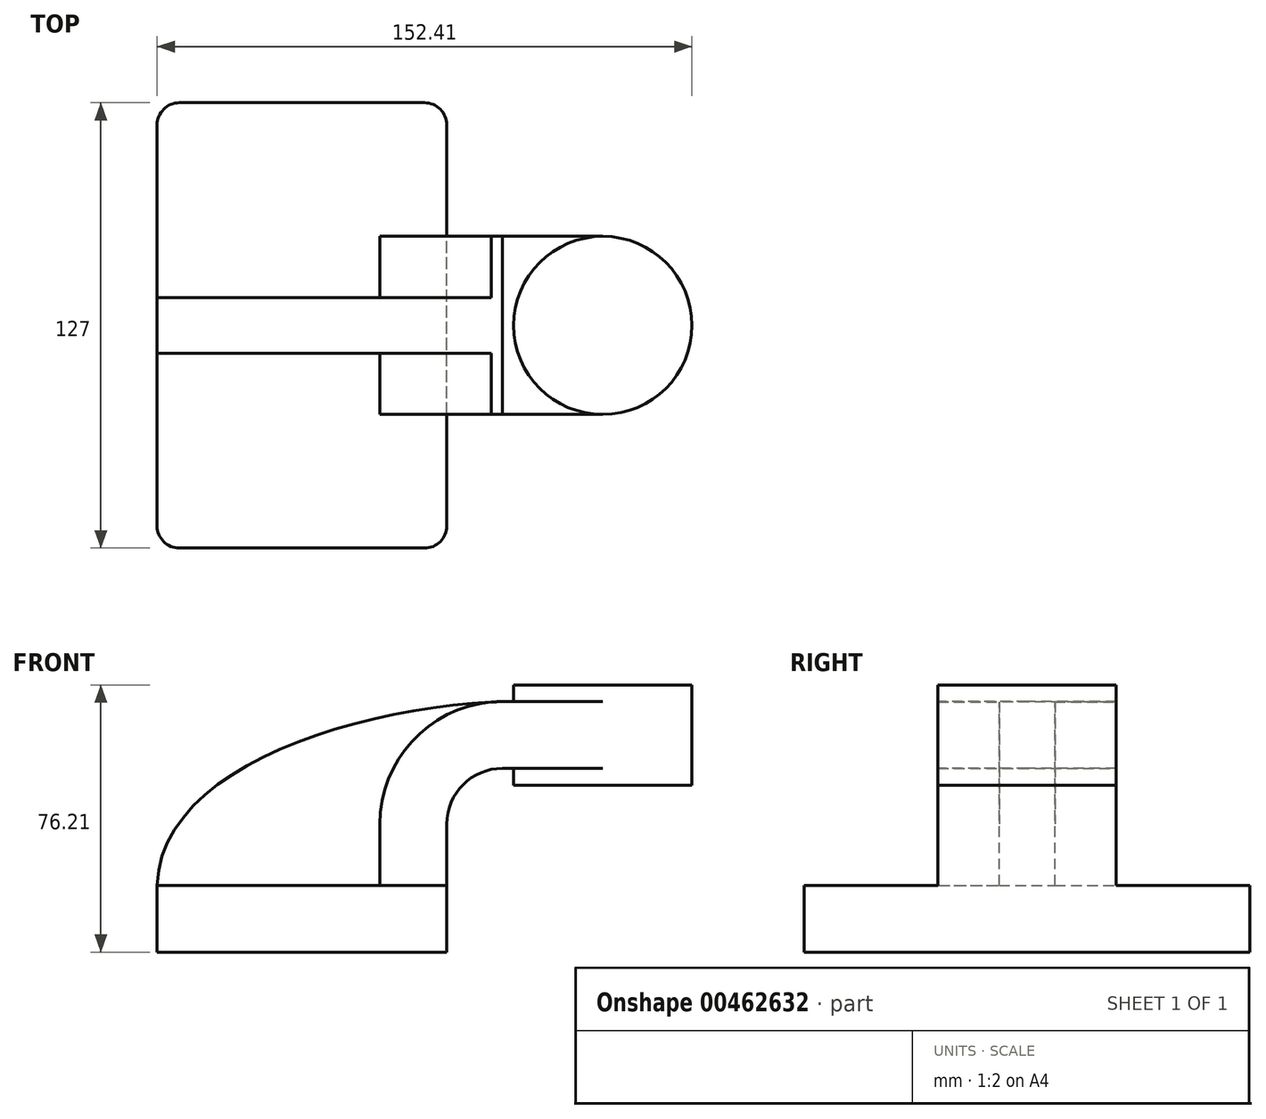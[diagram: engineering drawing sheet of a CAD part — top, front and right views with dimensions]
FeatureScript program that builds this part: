
annotation { "Feature Type Name" : "Feature", "Feature Type Description" : "" }
export const myFeature = defineFeature(function(context is Context, id is Id, definition is map)
    precondition{}
    {
        {
            var Q0;
            Q0=qCreatedBy(makeId("Front.planeOp"),FACE);
            var sketch = newSketch(context, id + "F0", { "sketchPlane" : qUnion([Q0])});
            skLineSegment(sketch, "E0.bottom", {"start": v(41.28, -9.52) * mm, "end": v(-41.28, -9.53) * mm});
            skLineSegment(sketch, "E0.top", {"start": v(41.28, 9.53) * mm, "end": v(-41.28, 9.53) * mm});
            skLineSegment(sketch, "E0.left", {"start": v(41.28, -9.52) * mm, "end": v(41.28, 9.53) * mm});
            skLineSegment(sketch, "E0.right", {"start": v(-41.28, -9.53) * mm, "end": v(-41.28, 9.53) * mm});
            skPoint(sketch, "E0.middle", {"position": v(0, 0) * mm});
            skLineSegment(sketch, "E1.bottom", {"start": v(60.33, 38.1) * mm, "end": v(111.13, 38.1) * mm});
            skLineSegment(sketch, "E1.top", {"start": v(60.33, 66.68) * mm, "end": v(111.13, 66.68) * mm});
            skLineSegment(sketch, "E1.left", {"start": v(60.33, 38.1) * mm, "end": v(60.33, 66.67) * mm});
            skLineSegment(sketch, "E1.right", {"start": v(111.13, 38.1) * mm, "end": v(111.13, 66.68) * mm});
            skPoint(sketch, "E1.middle", {"position": v(85.73, 52.39) * mm});
            skLineSegment(sketch, "E2", {"start": v(41.28, 9.53) * mm, "end": v(41.28, 27) * mm});
            skArc(sketch, "E3", {"start": v(41.27, 27) * mm, "mid": v(45.92, 38.23) * mm, "end": v(57.15, 42.88) * mm});
            skLineSegment(sketch, "E4", {"start": v(57.15, 42.88) * mm, "end": v(85.73, 42.88) * mm});
            skLineSegment(sketch, "E5.0", {"start": v(57.15, 61.93) * mm, "end": v(85.73, 61.93) * mm});
            skArc(sketch, "E5.1", {"start": v(22.23, 27) * mm, "mid": v(32.45, 51.7) * mm, "end": v(57.15, 61.93) * mm});
            skLineSegment(sketch, "E5.2", {"start": v(22.22, 9.53) * mm, "end": v(22.22, 27) * mm});
            skLineSegment(sketch, "E6", {"start": v(85.73, 38.1) * mm, "end": v(85.73, 66.68) * mm});
            skFitSpline(sketch, "E7", {"points": [v(-41.28, 9.53) * mm, v(57.15, 61.93) * mm], "startDerivative": vector(3.13, 101.9) * mm, "endDerivative": vector(124.2, 4.62) * mm});
            skSolve(sketch);
        }
        {
            var Q0;
            Q0=makeQuery(id+"F0.imprint","IMPRINT",FACE,{"disambiguationData":[TD([[makeQuery(id+"F0.imprint","IMPRINT",EDGE,{"derivedFrom":sQuery(id+"F0.wireOp",EDGE,"E0.bottom")}),-1.0]])]});
            extrude(context, id + "F1", {"entities" : qUnion([Q0]), "depth" : 127 * mm, "symmetric" : true});
        }
        {
            var Q0;
            {var subQ1=sQuery(id+"F0.wireOp",EDGE,"E2");Q0=makeQuery(id+"F0.imprint","IMPRINT",FACE,{"disambiguationData":[TD([[makeQuery(id+"F0.imprint","IMPRINT",EDGE,{"derivedFrom":subQ1}),1.0]])]});}
            var Q1;
            {var subQ0=sQuery(id+"F0.wireOp",EDGE,"E4");var subQ1=sQuery(id+"F0.wireOp",EDGE,"E1.left");var subQ2=makeQuery(id+"F0.imprint","INTERSECT",VERTEX,{"derivedFrom":[subQ1,subQ0]});Q1=makeQuery(id+"F0.imprint","IMPRINT",FACE,{"disambiguationData":[TD([[makeQuery(id+"F0.imprint","IMPRINT",EDGE,{"disambiguationData":[TD([[subQ2,-1.0]])],"derivedFrom":subQ1}),-1.0]])]});}
            extrude(context, id + "F2", {"entities" : qUnion([Q0, Q1]), "operationType" : NewBodyOperationType.ADD, "depth" : 50.8 * mm, "symmetric" : true});
        }
        {
            var Q0;
            {var subQ3=sQuery(id+"F0.wireOp",EDGE,"E5.2");Q0=makeQuery(id+"F0.imprint","IMPRINT",FACE,{"disambiguationData":[TD([[makeQuery(id+"F0.imprint","IMPRINT",EDGE,{"derivedFrom":subQ3}),1.0]])]});}
            extrude(context, id + "F3", {"entities" : qUnion([Q0]), "operationType" : NewBodyOperationType.ADD, "depth" : 15.88 * mm, "symmetric" : true});
        }
        {
            var Q0;
            {var subQ4=sQuery(id+"F0.wireOp",EDGE,"E1.right");Q0=makeQuery(id+"F0.imprint","IMPRINT",FACE,{"disambiguationData":[TD([[makeQuery(id+"F0.imprint","IMPRINT",EDGE,{"derivedFrom":subQ4}),1.0]])]});}
            var Q1;
            Q1=sQuery(id+"F0.wireOp",EDGE,"E6");
            revolve(context, id + "F4", {"operationType" : NewBodyOperationType.ADD, "entities" : qUnion([Q0]), "axis" : qUnion([Q1]), "revolveType" : RevolveType.FULL});
        }
        {
            var Q0;
            Q0=makeQuery(id+"F1.opExtrude","CAP_EDGE",EDGE,{"disambiguationData":[OSD([sQuery(id+"F0.wireOp",EDGE,"E0.left")])],"isStart":false});
            var Q1;
            Q1=makeQuery(id+"F1.opExtrude","CAP_EDGE",EDGE,{"disambiguationData":[OSD([sQuery(id+"F0.wireOp",EDGE,"E0.right")])],"isStart":false});
            var Q2;
            Q2=makeQuery(id+"F1.opExtrude","CAP_EDGE",EDGE,{"disambiguationData":[OSD([sQuery(id+"F0.wireOp",EDGE,"E0.left")])],"isStart":true});
            var Q3;
            Q3=makeQuery(id+"F1.opExtrude","CAP_EDGE",EDGE,{"disambiguationData":[OSD([sQuery(id+"F0.wireOp",EDGE,"E0.right")])],"isStart":true});
            fillet(context, id + "F5", {"entities" : qUnion([Q0, Q1, Q2, Q3]), "radius" : 6.35 * mm, "tangentPropagation" : true, "allowEdgeOverflow" : false});
        }
    });
